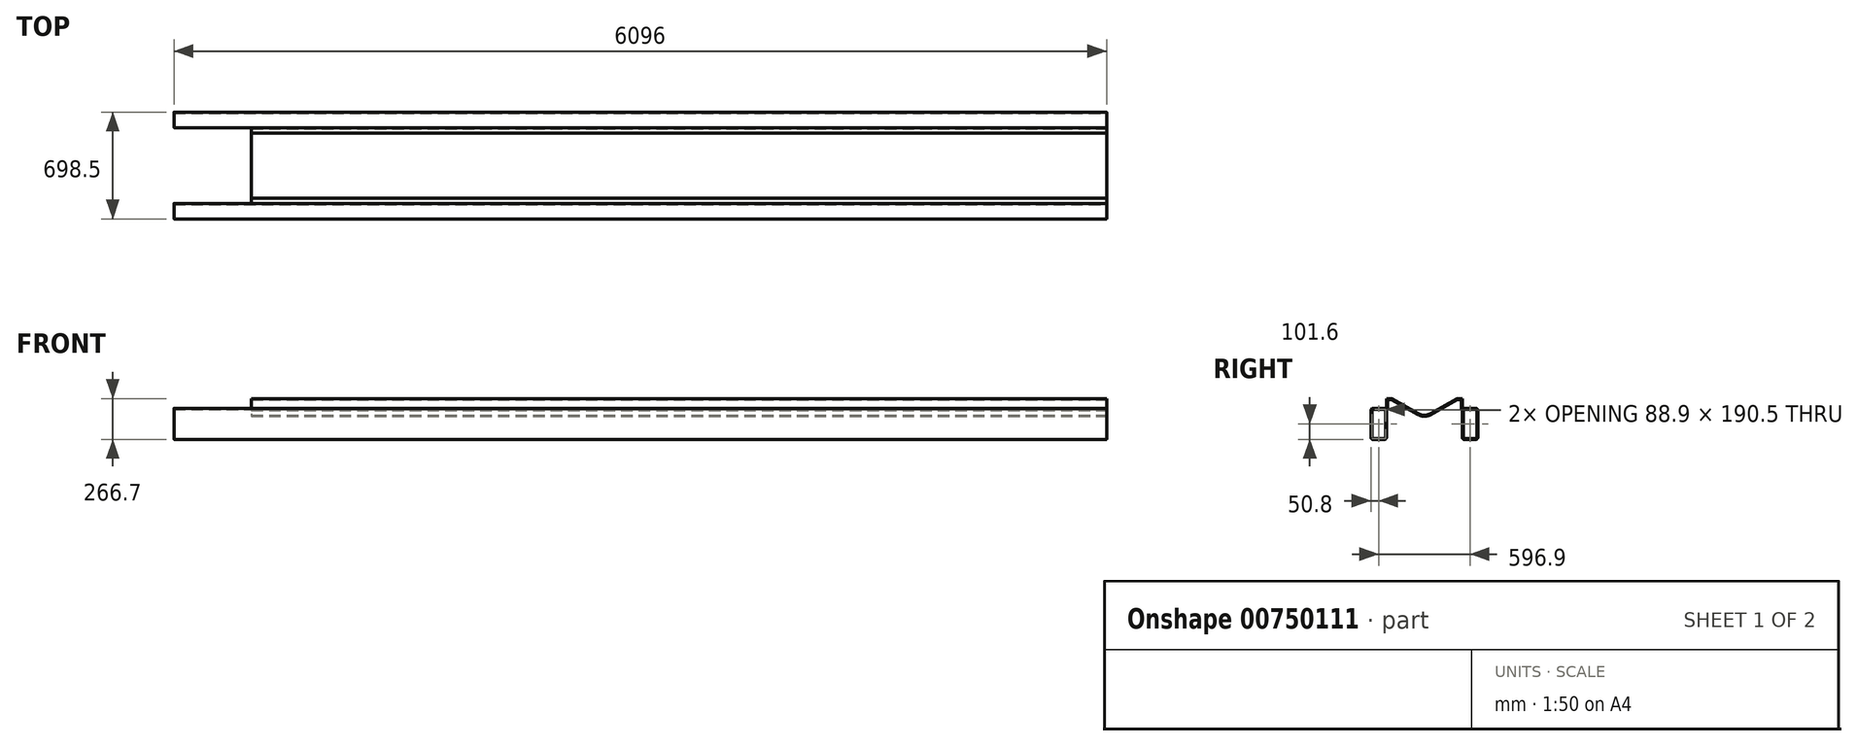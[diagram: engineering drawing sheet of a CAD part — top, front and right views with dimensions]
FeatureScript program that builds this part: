
annotation { "Feature Type Name" : "Feature", "Feature Type Description" : "" }
export const myFeature = defineFeature(function(context is Context, id is Id, definition is map)
    precondition{}
    {
        {
            var Q0;
            Q0=qCreatedBy(makeId("Right.planeOp"),FACE);
            var sketch = newSketch(context, id + "F0", { "sketchPlane" : qUnion([Q0])});
            skPoint(sketch, "E0", {"position": v(0, 0) * mm});
            skLineSegment(sketch, "E1", {"start": v(0, 228.65) * mm, "end": v(0, -305.7) * mm, "construction": true});
            skLineSegment(sketch, "E2.bottom", {"start": v(-336.55, 57.15) * mm, "end": v(-260.35, 57.15) * mm});
            skLineSegment(sketch, "E2.top", {"start": v(-336.55, -146.05) * mm, "end": v(-260.35, -146.05) * mm});
            skLineSegment(sketch, "E2.left", {"start": v(-349.25, 44.45) * mm, "end": v(-349.25, -133.35) * mm});
            skLineSegment(sketch, "E2.right", {"start": v(-247.65, 44.45) * mm, "end": v(-247.65, -133.35) * mm});
            skPoint(sketch, "E3.visualSharp", {"position": v(-247.65, 57.15) * mm});
            skArc(sketch, "E3.filletArc", {"start": v(-247.65, 44.45) * mm, "mid": v(-251.37, 53.43) * mm, "end": v(-260.35, 57.15) * mm});
            skPoint(sketch, "E4.visualSharp", {"position": v(-349.25, -146.05) * mm});
            skArc(sketch, "E4.filletArc", {"start": v(-349.25, -133.35) * mm, "mid": v(-345.53, -142.33) * mm, "end": v(-336.55, -146.05) * mm});
            skPoint(sketch, "E5.visualSharp", {"position": v(-247.65, -146.05) * mm});
            skArc(sketch, "E5.filletArc", {"start": v(-260.35, -146.05) * mm, "mid": v(-251.37, -142.33) * mm, "end": v(-247.65, -133.35) * mm});
            skPoint(sketch, "E6.visualSharp", {"position": v(-349.25, 57.15) * mm});
            skArc(sketch, "E6.filletArc", {"start": v(-336.55, 57.15) * mm, "mid": v(-345.53, 53.43) * mm, "end": v(-349.25, 44.45) * mm});
            skLineSegment(sketch, "E7.MirrorCS", {"start": v(247.65, 44.45) * mm, "end": v(247.65, -133.35) * mm});
            skArc(sketch, "E8.MirrorCS", {"start": v(247.65, 44.45) * mm, "mid": v(251.37, 53.43) * mm, "end": v(260.35, 57.15) * mm});
            skLineSegment(sketch, "E9.MirrorCS", {"start": v(336.55, 57.15) * mm, "end": v(260.35, 57.15) * mm});
            skArc(sketch, "E10.MirrorCS", {"start": v(336.55, 57.15) * mm, "mid": v(345.53, 53.43) * mm, "end": v(349.25, 44.45) * mm});
            skLineSegment(sketch, "E11.MirrorCS", {"start": v(349.25, 44.45) * mm, "end": v(349.25, -133.35) * mm});
            skArc(sketch, "E12.MirrorCS", {"start": v(349.25, -133.35) * mm, "mid": v(345.53, -142.33) * mm, "end": v(336.55, -146.05) * mm});
            skLineSegment(sketch, "E13.MirrorCS", {"start": v(336.55, -146.05) * mm, "end": v(260.35, -146.05) * mm});
            skPoint(sketch, "E14.MirrorP", {"position": v(247.65, -146.05) * mm});
            skArc(sketch, "E15.MirrorCS", {"start": v(260.35, -146.05) * mm, "mid": v(251.37, -142.33) * mm, "end": v(247.65, -133.35) * mm});
            skPoint(sketch, "E16.MirrorP", {"position": v(247.65, 57.15) * mm});
            skLineSegment(sketch, "E17", {"start": v(-213.12, 120.65) * mm, "end": v(-37.54, 21.25) * mm});
            skLineSegment(sketch, "E18.MirrorCS", {"start": v(213.12, 120.65) * mm, "end": v(37.54, 21.25) * mm});
            skLineSegment(sketch, "E19", {"start": v(-364.25, 120.65) * mm, "end": v(0, 120.65) * mm, "construction": true});
            skCircle(sketch, "E20", {"center": v(0, 218.9) * mm, "radius": 190.5 * mm, "construction": true});
            skArc(sketch, "E21.filletArc", {"start": v(-37.54, 21.25) * mm, "mid": v(0, 11.36) * mm, "end": v(37.54, 21.25) * mm});
            skCircle(sketch, "E22", {"center": v(0, 116.75) * mm, "radius": 101.6 * mm, "construction": true});
            skCircle(sketch, "E23", {"center": v(0, 61.3) * mm, "radius": 50.8 * mm, "construction": true});
            skArc(sketch, "E24.0", {"start": v(-336.55, 50.8) * mm, "mid": v(-341.04, 48.94) * mm, "end": v(-342.9, 44.45) * mm});
            skLineSegment(sketch, "E24.1", {"start": v(-342.9, 44.45) * mm, "end": v(-342.9, -133.35) * mm});
            skLineSegment(sketch, "E24.2", {"start": v(-336.55, 50.8) * mm, "end": v(-260.35, 50.8) * mm});
            skArc(sketch, "E24.3", {"start": v(-342.9, -133.35) * mm, "mid": v(-341.04, -137.84) * mm, "end": v(-336.55, -139.7) * mm});
            skArc(sketch, "E24.4", {"start": v(-254, 44.45) * mm, "mid": v(-255.86, 48.94) * mm, "end": v(-260.35, 50.8) * mm});
            skLineSegment(sketch, "E24.5", {"start": v(-254, 44.45) * mm, "end": v(-254, -133.35) * mm});
            skArc(sketch, "E24.6", {"start": v(-260.35, -139.7) * mm, "mid": v(-255.86, -137.84) * mm, "end": v(-254, -133.35) * mm});
            skLineSegment(sketch, "E24.7", {"start": v(-336.55, -139.7) * mm, "end": v(-260.35, -139.7) * mm});
            skArc(sketch, "E25.0", {"start": v(336.55, 50.8) * mm, "mid": v(341.04, 48.94) * mm, "end": v(342.9, 44.45) * mm});
            skLineSegment(sketch, "E25.1", {"start": v(342.9, 44.45) * mm, "end": v(342.9, -133.35) * mm});
            skLineSegment(sketch, "E25.2", {"start": v(336.55, 50.8) * mm, "end": v(260.35, 50.8) * mm});
            skArc(sketch, "E25.3", {"start": v(342.9, -133.35) * mm, "mid": v(341.04, -137.84) * mm, "end": v(336.55, -139.7) * mm});
            skArc(sketch, "E25.4", {"start": v(254, 44.45) * mm, "mid": v(255.86, 48.94) * mm, "end": v(260.35, 50.8) * mm});
            skLineSegment(sketch, "E25.5", {"start": v(254, 44.45) * mm, "end": v(254, -133.35) * mm});
            skArc(sketch, "E25.6", {"start": v(260.35, -139.7) * mm, "mid": v(255.86, -137.84) * mm, "end": v(254, -133.35) * mm});
            skLineSegment(sketch, "E25.7", {"start": v(336.55, -139.7) * mm, "end": v(260.35, -139.7) * mm});
            skLineSegment(sketch, "E26", {"start": v(-278.75, 57.15) * mm, "end": v(-269.35, 57.15) * mm});
            skLineSegment(sketch, "E27", {"start": v(-278.75, 57.15) * mm, "end": v(-268.14, 57.15) * mm});
            skLineSegment(sketch, "E28", {"start": v(-213.12, 120.65) * mm, "end": v(-247.65, 120.65) * mm});
            skLineSegment(sketch, "E29", {"start": v(-247.65, 120.65) * mm, "end": v(-247.65, 44.45) * mm});
            skLineSegment(sketch, "E30.MirrorCS", {"start": v(247.65, 120.65) * mm, "end": v(247.65, 44.45) * mm});
            skLineSegment(sketch, "E31", {"start": v(213.12, 120.65) * mm, "end": v(247.65, 120.65) * mm});
            skLineSegment(sketch, "E32.0", {"start": v(241.3, 114.3) * mm, "end": v(241.3, 44.45) * mm});
            skLineSegment(sketch, "E32.1", {"start": v(-216.25, 115.12) * mm, "end": v(-40.67, 15.73) * mm});
            skArc(sketch, "E32.2", {"start": v(-40.67, 15.73) * mm, "mid": v(0, 5.01) * mm, "end": v(40.67, 15.73) * mm});
            skLineSegment(sketch, "E32.3", {"start": v(214.8, 114.3) * mm, "end": v(40.67, 15.73) * mm});
            skLineSegment(sketch, "E32.4", {"start": v(214.8, 114.3) * mm, "end": v(241.3, 114.3) * mm});
            skLineSegment(sketch, "E33.MirrorCS", {"start": v(-241.3, 114.3) * mm, "end": v(-241.3, 44.45) * mm});
            skLineSegment(sketch, "E34.MirrorCS", {"start": v(-214.8, 114.3) * mm, "end": v(-241.3, 114.3) * mm});
            skLineSegment(sketch, "E35", {"start": v(-241.3, 44.45) * mm, "end": v(-247.65, 44.45) * mm});
            skLineSegment(sketch, "E36", {"start": v(241.3, 44.45) * mm, "end": v(247.65, 44.45) * mm});
            skSolve(sketch);
        }
        {
            var Q0;
            Q0=makeQuery(id+"F0.imprint","IMPRINT",FACE,{"disambiguationData":[TD([[makeQuery(id+"F0.imprint","IMPRINT",EDGE,{"derivedFrom":sQuery(id+"F0.wireOp",EDGE,"E2.top")}),1.0]])]});
            var Q1;
            Q1=makeQuery(id+"F0.imprint","IMPRINT",FACE,{"disambiguationData":[TD([[makeQuery(id+"F0.imprint","IMPRINT",EDGE,{"derivedFrom":sQuery(id+"F0.wireOp",EDGE,"E7.MirrorCS")}),1.0]])]});
            extrude(context, id + "F1", {"entities" : qUnion([Q0, Q1]), "oppositeDirection" : true, "depth" : 6096 * mm, "offsetDistance" : 25.4 * mm});
        }
        {
            var Q0;
            Q0=makeQuery(id+"F0.imprint","IMPRINT",FACE,{"disambiguationData":[TD([[makeQuery(id+"F0.imprint","IMPRINT",EDGE,{"derivedFrom":sQuery(id+"F0.wireOp",EDGE,"E17")}),-1.0]])]});
            var Q1;
            {var subQ4=sQuery(id+"F0.wireOp",EDGE,"40Ta9XpO-4Bih-OJ3X-wqKm-lZXZA3K83W1n");Q1=makeQuery(id+"F0.imprint","IMPRINT",FACE,{"disambiguationData":[TD([[makeQuery(id+"F0.imprint","IMPRINT",EDGE,{"derivedFrom":subQ4}),1.0]])]});}
            var Q2;
            {var subQ0=sQuery(id+"F0.wireOp",EDGE,"hLX8c9pQ-herN-AtC7-Xv8B-rJKkOfKo46Fv");Q2=makeQuery(id+"F0.imprint","IMPRINT",FACE,{"disambiguationData":[TD([[makeQuery(id+"F0.imprint","IMPRINT",EDGE,{"derivedFrom":subQ0}),-1.0]])]});}
            extrude(context, id + "F2", {"entities" : qUnion([Q0, Q1, Q2]), "oppositeDirection" : true, "depth" : 5588 * mm, "offsetDistance" : 25.4 * mm});
        }
    });
